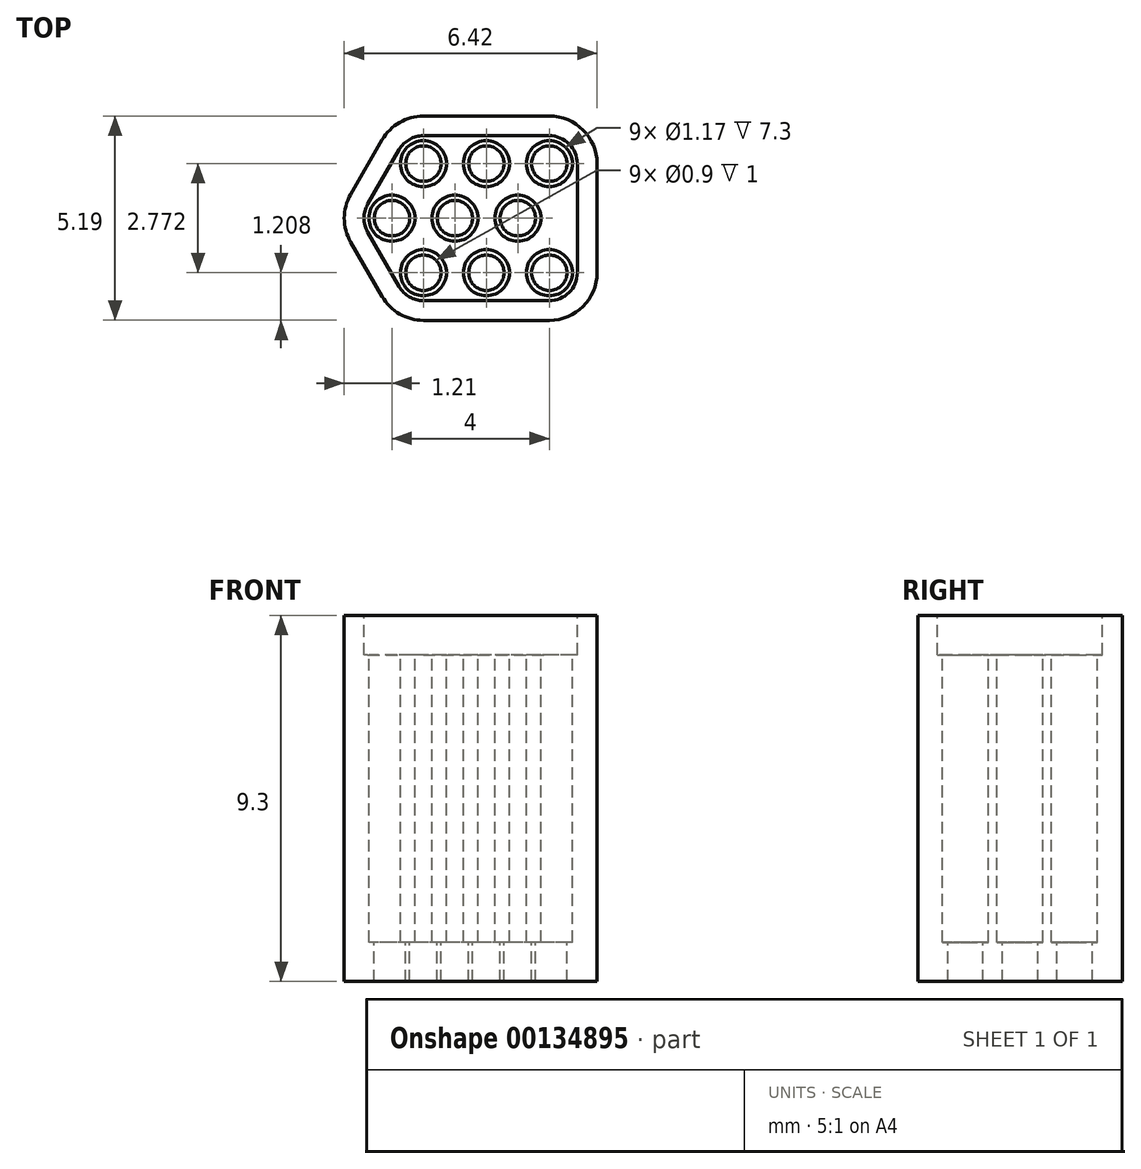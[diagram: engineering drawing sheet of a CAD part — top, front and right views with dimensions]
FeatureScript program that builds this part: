
annotation { "Feature Type Name" : "Feature", "Feature Type Description" : "" }
export const myFeature = defineFeature(function(context is Context, id is Id, definition is map)
    precondition{}
    {
        {
            var Q0;
            Q0=qCreatedBy(makeId("Top.planeOp"),FACE);
            var sketch = newSketch(context, id + "F0", { "sketchPlane" : qUnion([Q0])});
            skLineSegment(sketch, "E0", {"start": v(-0.8, 0) * mm, "end": v(-0.8, -4.2) * mm, "construction": true});
            skCircle(sketch, "E1", {"center": v(0, 0) * mm, "radius": 0.58 * mm});
            skCircle(sketch, "E2", {"center": v(0, -2.77) * mm, "radius": 0.58 * mm});
            skCircle(sketch, "E3", {"center": v(-0.8, -1.39) * mm, "radius": 0.58 * mm});
            skLineSegment(sketch, "E4", {"start": v(-4, -1.39) * mm, "end": v(-3.2, 0) * mm, "construction": true});
            skLineSegment(sketch, "E5", {"start": v(-3.2, 0) * mm, "end": v(0, 0) * mm, "construction": true});
            skLineSegment(sketch, "E6", {"start": v(0, 0) * mm, "end": v(0, -2.77) * mm, "construction": true});
            skLineSegment(sketch, "E7", {"start": v(-3.2, -2.77) * mm, "end": v(0, -2.77) * mm, "construction": true});
            skLineSegment(sketch, "E8", {"start": v(-3.2, -2.77) * mm, "end": v(-4, -1.39) * mm, "construction": true});
            skLineSegment(sketch, "E9.0", {"start": v(-3.6, -3.48) * mm, "end": v(-4.82, -1.39) * mm, "construction": true});
            skLineSegment(sketch, "E9.1", {"start": v(-3.6, 0.71) * mm, "end": v(0.71, 0.71) * mm, "construction": true});
            skLineSegment(sketch, "E9.2", {"start": v(0.71, 0.71) * mm, "end": v(0.71, -3.48) * mm, "construction": true});
            skLineSegment(sketch, "E9.3", {"start": v(-4.82, -1.39) * mm, "end": v(-3.6, 0.7) * mm, "construction": true});
            skLineSegment(sketch, "E9.5", {"start": v(-3.6, -3.48) * mm, "end": v(0.71, -3.48) * mm, "construction": true});
            skArc(sketch, "E10", {"start": v(-3.2, 0.7) * mm, "mid": v(-3.56, 0.61) * mm, "end": v(-3.81, 0.35) * mm});
            skArc(sketch, "E11", {"start": v(-4.61, -1.03) * mm, "mid": v(-4.71, -1.39) * mm, "end": v(-4.61, -1.74) * mm});
            skArc(sketch, "E12", {"start": v(-3.81, -3.13) * mm, "mid": v(-3.56, -3.39) * mm, "end": v(-3.2, -3.48) * mm});
            skArc(sketch, "E13", {"start": v(0, -3.48) * mm, "mid": v(0.5, -3.27) * mm, "end": v(0.7, -2.77) * mm});
            skArc(sketch, "E14", {"start": v(0.71, 0) * mm, "mid": v(0.5, 0.5) * mm, "end": v(0, 0.71) * mm});
            skLineSegment(sketch, "E15", {"start": v(-4.61, -1.03) * mm, "end": v(-3.81, 0.35) * mm});
            skLineSegment(sketch, "E16", {"start": v(-3.2, 0.71) * mm, "end": v(0, 0.71) * mm});
            skLineSegment(sketch, "E17", {"start": v(0.71, 0) * mm, "end": v(0.71, -2.77) * mm});
            skLineSegment(sketch, "E18", {"start": v(0, -3.48) * mm, "end": v(-3.2, -3.48) * mm});
            skLineSegment(sketch, "E19", {"start": v(-3.81, -3.13) * mm, "end": v(-4.61, -1.74) * mm});
            skArc(sketch, "E20.0", {"start": v(-3.2, 1.21) * mm, "mid": v(-3.8, 1.05) * mm, "end": v(-4.25, 0.6) * mm});
            skLineSegment(sketch, "E20.3", {"start": v(1.21, 0) * mm, "end": v(1.21, -2.77) * mm});
            skArc(sketch, "E20.4", {"start": v(1.21, 0) * mm, "mid": v(0.86, 0.86) * mm, "end": v(0, 1.21) * mm});
            skArc(sketch, "E20.5", {"start": v(0, -3.98) * mm, "mid": v(0.86, -3.63) * mm, "end": v(1.2, -2.77) * mm});
            skLineSegment(sketch, "E20.6", {"start": v(-3.2, 1.2) * mm, "end": v(0, 1.21) * mm});
            skLineSegment(sketch, "E20.7", {"start": v(0, -3.98) * mm, "end": v(-3.2, -3.98) * mm});
            skArc(sketch, "E20.8", {"start": v(-4.25, -3.38) * mm, "mid": v(-3.8, -3.82) * mm, "end": v(-3.2, -3.98) * mm});
            skLineSegment(sketch, "E20.9", {"start": v(-4.25, -3.38) * mm, "end": v(-5.05, -2) * mm});
            skArc(sketch, "E20.10", {"start": v(-5.05, -0.78) * mm, "mid": v(-5.2, -1.39) * mm, "end": v(-5.05, -2) * mm});
            skLineSegment(sketch, "E20.11", {"start": v(-5.05, -0.78) * mm, "end": v(-4.25, 0.6) * mm});
            skCircle(sketch, "E21.1.0.0", {"center": v(-1.6, -2.77) * mm, "radius": 0.58 * mm});
            skCircle(sketch, "E21.1.0.1", {"center": v(-2.4, -1.39) * mm, "radius": 0.58 * mm});
            skCircle(sketch, "E21.1.0.2", {"center": v(-1.6, 0) * mm, "radius": 0.58 * mm});
            skCircle(sketch, "E21.2.0.0", {"center": v(-3.2, -2.77) * mm, "radius": 0.58 * mm});
            skCircle(sketch, "E21.2.0.1", {"center": v(-4, -1.39) * mm, "radius": 0.58 * mm});
            skCircle(sketch, "E21.2.0.2", {"center": v(-3.2, 0) * mm, "radius": 0.58 * mm});
            skLineSegment(sketch, "E21.direction1", {"start": v(0, -2.77) * mm, "end": v(-1.6, -2.77) * mm, "construction": true});
            skSolve(sketch);
        }
        {
            var Q0;
            Q0=makeQuery(id+"F0.imprint","IMPRINT",FACE,{"disambiguationData":[TD([[makeQuery(id+"F0.imprint","IMPRINT",EDGE,{"derivedFrom":sQuery(id+"F0.wireOp",EDGE,"E10")}),-1.0]])]});
            var Q1;
            Q1=makeQuery(id+"F0.imprint","IMPRINT",FACE,{"disambiguationData":[TD([[makeQuery(id+"F0.imprint","IMPRINT",EDGE,{"derivedFrom":sQuery(id+"F0.wireOp",EDGE,"E1")}),-1.0]])]});
            var Q2;
            Q2=makeQuery(id+"F0.imprint","IMPRINT",FACE,{"disambiguationData":[TD([[makeQuery(id+"F0.imprint","IMPRINT",EDGE,{"derivedFrom":sQuery(id+"F0.wireOp",EDGE,"E21.2.0.1")}),1.0]])]});
            var Q3;
            Q3=makeQuery(id+"F0.imprint","IMPRINT",FACE,{"disambiguationData":[TD([[makeQuery(id+"F0.imprint","IMPRINT",EDGE,{"derivedFrom":sQuery(id+"F0.wireOp",EDGE,"E21.2.0.2")}),1.0]])]});
            var Q4;
            Q4=makeQuery(id+"F0.imprint","IMPRINT",FACE,{"disambiguationData":[TD([[makeQuery(id+"F0.imprint","IMPRINT",EDGE,{"derivedFrom":sQuery(id+"F0.wireOp",EDGE,"E21.1.0.2")}),1.0]])]});
            var Q5;
            Q5=makeQuery(id+"F0.imprint","IMPRINT",FACE,{"disambiguationData":[TD([[makeQuery(id+"F0.imprint","IMPRINT",EDGE,{"derivedFrom":sQuery(id+"F0.wireOp",EDGE,"E21.1.0.1")}),1.0]])]});
            var Q6;
            Q6=makeQuery(id+"F0.imprint","IMPRINT",FACE,{"disambiguationData":[TD([[makeQuery(id+"F0.imprint","IMPRINT",EDGE,{"derivedFrom":sQuery(id+"F0.wireOp",EDGE,"E21.2.0.0")}),1.0]])]});
            var Q7;
            Q7=makeQuery(id+"F0.imprint","IMPRINT",FACE,{"disambiguationData":[TD([[makeQuery(id+"F0.imprint","IMPRINT",EDGE,{"derivedFrom":sQuery(id+"F0.wireOp",EDGE,"E21.1.0.0")}),1.0]])]});
            var Q8;
            Q8=makeQuery(id+"F0.imprint","IMPRINT",FACE,{"disambiguationData":[TD([[makeQuery(id+"F0.imprint","IMPRINT",EDGE,{"derivedFrom":sQuery(id+"F0.wireOp",EDGE,"E3")}),1.0]])]});
            var Q9;
            Q9=makeQuery(id+"F0.imprint","IMPRINT",FACE,{"disambiguationData":[TD([[makeQuery(id+"F0.imprint","IMPRINT",EDGE,{"derivedFrom":sQuery(id+"F0.wireOp",EDGE,"E1")}),1.0]])]});
            var Q10;
            Q10=makeQuery(id+"F0.imprint","IMPRINT",FACE,{"disambiguationData":[TD([[makeQuery(id+"F0.imprint","IMPRINT",EDGE,{"derivedFrom":sQuery(id+"F0.wireOp",EDGE,"E2")}),1.0]])]});
            extrude(context, id + "F1", {"entities" : qUnion([Q0, Q1, Q2, Q3, Q4, Q5, Q6, Q7, Q8, Q9, Q10]), "oppositeDirection" : true, "depth" : 9.3 * mm});
        }
        {
            var Q0;
            Q0=makeQuery(id+"F0.imprint","IMPRINT",FACE,{"disambiguationData":[TD([[makeQuery(id+"F0.imprint","IMPRINT",EDGE,{"derivedFrom":sQuery(id+"F0.wireOp",EDGE,"E1")}),-1.0]])]});
            var Q1;
            Q1=makeQuery(id+"F0.imprint","IMPRINT",FACE,{"disambiguationData":[TD([[makeQuery(id+"F0.imprint","IMPRINT",EDGE,{"derivedFrom":sQuery(id+"F0.wireOp",EDGE,"a57e1848-316f-4acb-9686-28404833bcae.3.0.0")}),1.0]])]});
            var Q2;
            Q2=makeQuery(id+"F0.imprint","IMPRINT",FACE,{"disambiguationData":[TD([[makeQuery(id+"F0.imprint","IMPRINT",EDGE,{"derivedFrom":sQuery(id+"F0.wireOp",EDGE,"a57e1848-316f-4acb-9686-28404833bcae.3.0.1")}),1.0]])]});
            var Q3;
            Q3=makeQuery(id+"F0.imprint","IMPRINT",FACE,{"disambiguationData":[TD([[makeQuery(id+"F0.imprint","IMPRINT",EDGE,{"derivedFrom":sQuery(id+"F0.wireOp",EDGE,"e6241aa5-61be-4e4d-b619-a7d30d87e54e.1.0.0")}),1.0]])]});
            var Q4;
            Q4=makeQuery(id+"F0.imprint","IMPRINT",FACE,{"disambiguationData":[TD([[makeQuery(id+"F0.imprint","IMPRINT",EDGE,{"derivedFrom":sQuery(id+"F0.wireOp",EDGE,"a57e1848-316f-4acb-9686-28404833bcae.3.0.2")}),1.0]])]});
            var Q5;
            Q5=makeQuery(id+"F0.imprint","IMPRINT",FACE,{"disambiguationData":[TD([[makeQuery(id+"F0.imprint","IMPRINT",EDGE,{"derivedFrom":sQuery(id+"F0.wireOp",EDGE,"a57e1848-316f-4acb-9686-28404833bcae.3.0.3")}),1.0]])]});
            var Q6;
            Q6=makeQuery(id+"F0.imprint","IMPRINT",FACE,{"disambiguationData":[TD([[makeQuery(id+"F0.imprint","IMPRINT",EDGE,{"derivedFrom":sQuery(id+"F0.wireOp",EDGE,"a57e1848-316f-4acb-9686-28404833bcae.2.0.2")}),1.0]])]});
            var Q7;
            Q7=makeQuery(id+"F0.imprint","IMPRINT",FACE,{"disambiguationData":[TD([[makeQuery(id+"F0.imprint","IMPRINT",EDGE,{"derivedFrom":sQuery(id+"F0.wireOp",EDGE,"a57e1848-316f-4acb-9686-28404833bcae.2.0.1")}),1.0]])]});
            var Q8;
            Q8=makeQuery(id+"F0.imprint","IMPRINT",FACE,{"disambiguationData":[TD([[makeQuery(id+"F0.imprint","IMPRINT",EDGE,{"derivedFrom":sQuery(id+"F0.wireOp",EDGE,"a57e1848-316f-4acb-9686-28404833bcae.2.0.0")}),1.0]])]});
            var Q9;
            Q9=makeQuery(id+"F0.imprint","IMPRINT",FACE,{"disambiguationData":[TD([[makeQuery(id+"F0.imprint","IMPRINT",EDGE,{"derivedFrom":sQuery(id+"F0.wireOp",EDGE,"a57e1848-316f-4acb-9686-28404833bcae.1.0.0")}),1.0]])]});
            var Q10;
            Q10=makeQuery(id+"F0.imprint","IMPRINT",FACE,{"disambiguationData":[TD([[makeQuery(id+"F0.imprint","IMPRINT",EDGE,{"derivedFrom":sQuery(id+"F0.wireOp",EDGE,"a57e1848-316f-4acb-9686-28404833bcae.1.0.1")}),1.0]])]});
            var Q11;
            Q11=makeQuery(id+"F0.imprint","IMPRINT",FACE,{"disambiguationData":[TD([[makeQuery(id+"F0.imprint","IMPRINT",EDGE,{"derivedFrom":sQuery(id+"F0.wireOp",EDGE,"a57e1848-316f-4acb-9686-28404833bcae.2.0.3")}),1.0]])]});
            var Q12;
            Q12=makeQuery(id+"F0.imprint","IMPRINT",FACE,{"disambiguationData":[TD([[makeQuery(id+"F0.imprint","IMPRINT",EDGE,{"derivedFrom":sQuery(id+"F0.wireOp",EDGE,"a57e1848-316f-4acb-9686-28404833bcae.1.0.2")}),1.0]])]});
            var Q13;
            Q13=makeQuery(id+"F0.imprint","IMPRINT",FACE,{"disambiguationData":[TD([[makeQuery(id+"F0.imprint","IMPRINT",EDGE,{"derivedFrom":sQuery(id+"F0.wireOp",EDGE,"E1")}),1.0]])]});
            var Q14;
            Q14=makeQuery(id+"F0.imprint","IMPRINT",FACE,{"disambiguationData":[TD([[makeQuery(id+"F0.imprint","IMPRINT",EDGE,{"derivedFrom":sQuery(id+"F0.wireOp",EDGE,"E3")}),1.0]])]});
            var Q15;
            Q15=makeQuery(id+"F0.imprint","IMPRINT",FACE,{"disambiguationData":[TD([[makeQuery(id+"F0.imprint","IMPRINT",EDGE,{"derivedFrom":sQuery(id+"F0.wireOp",EDGE,"a57e1848-316f-4acb-9686-28404833bcae.1.0.3")}),1.0]])]});
            var Q16;
            Q16=makeQuery(id+"F0.imprint","IMPRINT",FACE,{"disambiguationData":[TD([[makeQuery(id+"F0.imprint","IMPRINT",EDGE,{"derivedFrom":sQuery(id+"F0.wireOp",EDGE,"nBaw7tlR-HIxs-2q5P-bhm3-oVcILwCY4JMG")}),1.0]])]});
            var Q17;
            Q17=makeQuery(id+"F0.imprint","IMPRINT",FACE,{"disambiguationData":[TD([[makeQuery(id+"F0.imprint","IMPRINT",EDGE,{"derivedFrom":sQuery(id+"F0.wireOp",EDGE,"E2")}),1.0]])]});
            var Q18;
            Q18=makeQuery(id+"F0.imprint","IMPRINT",FACE,{"disambiguationData":[TD([[makeQuery(id+"F0.imprint","IMPRINT",EDGE,{"derivedFrom":sQuery(id+"F0.wireOp",EDGE,"E21.2.0.1")}),1.0]])]});
            var Q19;
            Q19=makeQuery(id+"F0.imprint","IMPRINT",FACE,{"disambiguationData":[TD([[makeQuery(id+"F0.imprint","IMPRINT",EDGE,{"derivedFrom":sQuery(id+"F0.wireOp",EDGE,"E21.1.0.1")}),1.0]])]});
            var Q20;
            Q20=makeQuery(id+"F0.imprint","IMPRINT",FACE,{"disambiguationData":[TD([[makeQuery(id+"F0.imprint","IMPRINT",EDGE,{"derivedFrom":sQuery(id+"F0.wireOp",EDGE,"E21.2.0.2")}),1.0]])]});
            var Q21;
            Q21=makeQuery(id+"F0.imprint","IMPRINT",FACE,{"disambiguationData":[TD([[makeQuery(id+"F0.imprint","IMPRINT",EDGE,{"derivedFrom":sQuery(id+"F0.wireOp",EDGE,"E21.1.0.2")}),1.0]])]});
            var Q22;
            Q22=makeQuery(id+"F0.imprint","IMPRINT",FACE,{"disambiguationData":[TD([[makeQuery(id+"F0.imprint","IMPRINT",EDGE,{"derivedFrom":sQuery(id+"F0.wireOp",EDGE,"E21.1.0.0")}),1.0]])]});
            var Q23;
            Q23=makeQuery(id+"F0.imprint","IMPRINT",FACE,{"disambiguationData":[TD([[makeQuery(id+"F0.imprint","IMPRINT",EDGE,{"derivedFrom":sQuery(id+"F0.wireOp",EDGE,"E21.2.0.0")}),1.0]])]});
            extrude(context, id + "F2", {"entities" : qUnion([Q0, Q1, Q2, Q3, Q4, Q5, Q6, Q7, Q8, Q9, Q10, Q11, Q12, Q13, Q14, Q15, Q16, Q17, Q18, Q19, Q20, Q21, Q22, Q23]), "operationType" : NewBodyOperationType.REMOVE, "oppositeDirection" : true, "depth" : 1 * mm});
        }
        {
            var Q0;
            Q0=makeQuery(id+"F0.imprint","IMPRINT",FACE,{"disambiguationData":[TD([[makeQuery(id+"F0.imprint","IMPRINT",EDGE,{"derivedFrom":sQuery(id+"F0.wireOp",EDGE,"e6241aa5-61be-4e4d-b619-a7d30d87e54e.1.0.0")}),1.0]])]});
            var Q1;
            Q1=makeQuery(id+"F0.imprint","IMPRINT",FACE,{"disambiguationData":[TD([[makeQuery(id+"F0.imprint","IMPRINT",EDGE,{"derivedFrom":sQuery(id+"F0.wireOp",EDGE,"a57e1848-316f-4acb-9686-28404833bcae.3.0.1")}),1.0]])]});
            var Q2;
            Q2=makeQuery(id+"F0.imprint","IMPRINT",FACE,{"disambiguationData":[TD([[makeQuery(id+"F0.imprint","IMPRINT",EDGE,{"derivedFrom":sQuery(id+"F0.wireOp",EDGE,"a57e1848-316f-4acb-9686-28404833bcae.3.0.0")}),1.0]])]});
            var Q3;
            Q3=makeQuery(id+"F0.imprint","IMPRINT",FACE,{"disambiguationData":[TD([[makeQuery(id+"F0.imprint","IMPRINT",EDGE,{"derivedFrom":sQuery(id+"F0.wireOp",EDGE,"a57e1848-316f-4acb-9686-28404833bcae.3.0.2")}),1.0]])]});
            var Q4;
            Q4=makeQuery(id+"F0.imprint","IMPRINT",FACE,{"disambiguationData":[TD([[makeQuery(id+"F0.imprint","IMPRINT",EDGE,{"derivedFrom":sQuery(id+"F0.wireOp",EDGE,"a57e1848-316f-4acb-9686-28404833bcae.3.0.3")}),1.0]])]});
            var Q5;
            Q5=makeQuery(id+"F0.imprint","IMPRINT",FACE,{"disambiguationData":[TD([[makeQuery(id+"F0.imprint","IMPRINT",EDGE,{"derivedFrom":sQuery(id+"F0.wireOp",EDGE,"a57e1848-316f-4acb-9686-28404833bcae.2.0.1")}),1.0]])]});
            var Q6;
            Q6=makeQuery(id+"F0.imprint","IMPRINT",FACE,{"disambiguationData":[TD([[makeQuery(id+"F0.imprint","IMPRINT",EDGE,{"derivedFrom":sQuery(id+"F0.wireOp",EDGE,"a57e1848-316f-4acb-9686-28404833bcae.2.0.0")}),1.0]])]});
            var Q7;
            Q7=makeQuery(id+"F0.imprint","IMPRINT",FACE,{"disambiguationData":[TD([[makeQuery(id+"F0.imprint","IMPRINT",EDGE,{"derivedFrom":sQuery(id+"F0.wireOp",EDGE,"a57e1848-316f-4acb-9686-28404833bcae.1.0.0")}),1.0]])]});
            var Q8;
            Q8=makeQuery(id+"F0.imprint","IMPRINT",FACE,{"disambiguationData":[TD([[makeQuery(id+"F0.imprint","IMPRINT",EDGE,{"derivedFrom":sQuery(id+"F0.wireOp",EDGE,"a57e1848-316f-4acb-9686-28404833bcae.1.0.1")}),1.0]])]});
            var Q9;
            Q9=makeQuery(id+"F0.imprint","IMPRINT",FACE,{"disambiguationData":[TD([[makeQuery(id+"F0.imprint","IMPRINT",EDGE,{"derivedFrom":sQuery(id+"F0.wireOp",EDGE,"a57e1848-316f-4acb-9686-28404833bcae.2.0.3")}),1.0]])]});
            var Q10;
            Q10=makeQuery(id+"F0.imprint","IMPRINT",FACE,{"disambiguationData":[TD([[makeQuery(id+"F0.imprint","IMPRINT",EDGE,{"derivedFrom":sQuery(id+"F0.wireOp",EDGE,"a57e1848-316f-4acb-9686-28404833bcae.2.0.2")}),1.0]])]});
            var Q11;
            Q11=makeQuery(id+"F0.imprint","IMPRINT",FACE,{"disambiguationData":[TD([[makeQuery(id+"F0.imprint","IMPRINT",EDGE,{"derivedFrom":sQuery(id+"F0.wireOp",EDGE,"a57e1848-316f-4acb-9686-28404833bcae.1.0.2")}),1.0]])]});
            var Q12;
            Q12=makeQuery(id+"F0.imprint","IMPRINT",FACE,{"disambiguationData":[TD([[makeQuery(id+"F0.imprint","IMPRINT",EDGE,{"derivedFrom":sQuery(id+"F0.wireOp",EDGE,"a57e1848-316f-4acb-9686-28404833bcae.1.0.3")}),1.0]])]});
            var Q13;
            Q13=makeQuery(id+"F0.imprint","IMPRINT",FACE,{"disambiguationData":[TD([[makeQuery(id+"F0.imprint","IMPRINT",EDGE,{"derivedFrom":sQuery(id+"F0.wireOp",EDGE,"E3")}),1.0]])]});
            var Q14;
            Q14=makeQuery(id+"F0.imprint","IMPRINT",FACE,{"disambiguationData":[TD([[makeQuery(id+"F0.imprint","IMPRINT",EDGE,{"derivedFrom":sQuery(id+"F0.wireOp",EDGE,"E1")}),1.0]])]});
            var Q15;
            Q15=makeQuery(id+"F0.imprint","IMPRINT",FACE,{"disambiguationData":[TD([[makeQuery(id+"F0.imprint","IMPRINT",EDGE,{"derivedFrom":sQuery(id+"F0.wireOp",EDGE,"E2")}),1.0]])]});
            var Q16;
            Q16=makeQuery(id+"F0.imprint","IMPRINT",FACE,{"disambiguationData":[TD([[makeQuery(id+"F0.imprint","IMPRINT",EDGE,{"derivedFrom":sQuery(id+"F0.wireOp",EDGE,"nBaw7tlR-HIxs-2q5P-bhm3-oVcILwCY4JMG")}),1.0]])]});
            var Q17;
            Q17=makeQuery(id+"F0.imprint","IMPRINT",FACE,{"disambiguationData":[TD([[makeQuery(id+"F0.imprint","IMPRINT",EDGE,{"derivedFrom":sQuery(id+"F0.wireOp",EDGE,"nBaw7tlR-HIxs-2q5P-bhm3-oVcILwCY4JMG")}),1.0]])]});
            var Q18;
            Q18=makeQuery(id+"F0.imprint","IMPRINT",FACE,{"disambiguationData":[TD([[makeQuery(id+"F0.imprint","IMPRINT",EDGE,{"derivedFrom":sQuery(id+"F0.wireOp",EDGE,"a57e1848-316f-4acb-9686-28404833bcae.2.0.2")}),1.0]])]});
            var Q19;
            Q19=makeQuery(id+"F0.imprint","IMPRINT",FACE,{"disambiguationData":[TD([[makeQuery(id+"F0.imprint","IMPRINT",EDGE,{"derivedFrom":sQuery(id+"F0.wireOp",EDGE,"a57e1848-316f-4acb-9686-28404833bcae.1.0.2")}),1.0]])]});
            var Q20;
            Q20=makeQuery(id+"F0.imprint","IMPRINT",FACE,{"disambiguationData":[TD([[makeQuery(id+"F0.imprint","IMPRINT",EDGE,{"derivedFrom":sQuery(id+"F0.wireOp",EDGE,"a57e1848-316f-4acb-9686-28404833bcae.1.0.3")}),1.0]])]});
            var Q21;
            Q21=makeQuery(id+"F0.imprint","IMPRINT",FACE,{"disambiguationData":[TD([[makeQuery(id+"F0.imprint","IMPRINT",EDGE,{"derivedFrom":sQuery(id+"F0.wireOp",EDGE,"E3")}),1.0]])]});
            var Q22;
            Q22=makeQuery(id+"F0.imprint","IMPRINT",FACE,{"disambiguationData":[TD([[makeQuery(id+"F0.imprint","IMPRINT",EDGE,{"derivedFrom":sQuery(id+"F0.wireOp",EDGE,"E1")}),1.0]])]});
            var Q23;
            Q23=makeQuery(id+"F0.imprint","IMPRINT",FACE,{"disambiguationData":[TD([[makeQuery(id+"F0.imprint","IMPRINT",EDGE,{"derivedFrom":sQuery(id+"F0.wireOp",EDGE,"E2")}),1.0]])]});
            var Q24;
            Q24=makeQuery(id+"F0.imprint","IMPRINT",FACE,{"disambiguationData":[TD([[makeQuery(id+"F0.imprint","IMPRINT",EDGE,{"derivedFrom":sQuery(id+"F0.wireOp",EDGE,"nBaw7tlR-HIxs-2q5P-bhm3-oVcILwCY4JMG")}),1.0]])]});
            var Q25;
            Q25=makeQuery(id+"F0.imprint","IMPRINT",FACE,{"disambiguationData":[TD([[makeQuery(id+"F0.imprint","IMPRINT",EDGE,{"derivedFrom":sQuery(id+"F0.wireOp",EDGE,"E21.1.0.0")}),1.0]])]});
            var Q26;
            Q26=makeQuery(id+"F0.imprint","IMPRINT",FACE,{"disambiguationData":[TD([[makeQuery(id+"F0.imprint","IMPRINT",EDGE,{"derivedFrom":sQuery(id+"F0.wireOp",EDGE,"E21.2.0.0")}),1.0]])]});
            var Q27;
            Q27=makeQuery(id+"F0.imprint","IMPRINT",FACE,{"disambiguationData":[TD([[makeQuery(id+"F0.imprint","IMPRINT",EDGE,{"derivedFrom":sQuery(id+"F0.wireOp",EDGE,"E21.1.0.1")}),1.0]])]});
            var Q28;
            Q28=makeQuery(id+"F0.imprint","IMPRINT",FACE,{"disambiguationData":[TD([[makeQuery(id+"F0.imprint","IMPRINT",EDGE,{"derivedFrom":sQuery(id+"F0.wireOp",EDGE,"E21.1.0.2")}),1.0]])]});
            var Q29;
            Q29=makeQuery(id+"F0.imprint","IMPRINT",FACE,{"disambiguationData":[TD([[makeQuery(id+"F0.imprint","IMPRINT",EDGE,{"derivedFrom":sQuery(id+"F0.wireOp",EDGE,"E21.2.0.2")}),1.0]])]});
            var Q30;
            Q30=makeQuery(id+"F0.imprint","IMPRINT",FACE,{"disambiguationData":[TD([[makeQuery(id+"F0.imprint","IMPRINT",EDGE,{"derivedFrom":sQuery(id+"F0.wireOp",EDGE,"E21.2.0.1")}),1.0]])]});
            extrude(context, id + "F3", {"entities" : qUnion([Q0, Q1, Q2, Q3, Q4, Q5, Q6, Q7, Q8, Q9, Q10, Q11, Q12, Q13, Q14, Q15, Q16, Q17, Q18, Q19, Q20, Q21, Q22, Q23, Q24, Q25, Q26, Q27, Q28, Q29, Q30]), "operationType" : NewBodyOperationType.REMOVE, "oppositeDirection" : true, "depth" : 8.3 * mm});
        }
        {
            var Q0;
            Q0=qCreatedBy(makeId("Top.planeOp"),FACE);
            var sketch = newSketch(context, id + "F4", { "sketchPlane" : qUnion([Q0])});
            skLineSegment(sketch, "E22", {"start": v(-0.8, 0) * mm, "end": v(-0.8, -4.16) * mm, "construction": true});
            skCircle(sketch, "E23", {"center": v(0, 0) * mm, "radius": 0.58 * mm, "construction": true});
            skCircle(sketch, "E24", {"center": v(0, -2.77) * mm, "radius": 0.58 * mm, "construction": true});
            skCircle(sketch, "E25", {"center": v(-0.8, -1.39) * mm, "radius": 0.58 * mm, "construction": true});
            skCircle(sketch, "E26", {"center": v(-0.8, -4.16) * mm, "radius": 0.58 * mm, "construction": true});
            skCircle(sketch, "E27.1.0.0", {"center": v(-1.6, 0) * mm, "radius": 0.58 * mm, "construction": true});
            skCircle(sketch, "E27.1.0.1", {"center": v(-2.4, -1.39) * mm, "radius": 0.58 * mm, "construction": true});
            skCircle(sketch, "E27.1.0.2", {"center": v(-2.4, -4.16) * mm, "radius": 0.58 * mm, "construction": true});
            skCircle(sketch, "E27.1.0.3", {"center": v(-1.6, -2.77) * mm, "radius": 0.58 * mm, "construction": true});
            skCircle(sketch, "E27.2.0.0", {"center": v(-3.2, 0) * mm, "radius": 0.58 * mm, "construction": true});
            skCircle(sketch, "E27.2.0.1", {"center": v(-4, -1.39) * mm, "radius": 0.58 * mm, "construction": true});
            skCircle(sketch, "E27.2.0.2", {"center": v(-4, -4.16) * mm, "radius": 0.58 * mm, "construction": true});
            skCircle(sketch, "E27.2.0.3", {"center": v(-3.2, -2.77) * mm, "radius": 0.58 * mm, "construction": true});
            skCircle(sketch, "E27.3.0.0", {"center": v(-4.8, 0) * mm, "radius": 0.58 * mm, "construction": true});
            skCircle(sketch, "E27.3.0.1", {"center": v(-5.6, -1.39) * mm, "radius": 0.58 * mm, "construction": true});
            skCircle(sketch, "E27.3.0.2", {"center": v(-5.6, -4.16) * mm, "radius": 0.58 * mm, "construction": true});
            skCircle(sketch, "E27.3.0.3", {"center": v(-4.8, -2.77) * mm, "radius": 0.58 * mm, "construction": true});
            skLineSegment(sketch, "E27.direction1", {"start": v(-0.8, -4.16) * mm, "end": v(-2.4, -4.16) * mm, "construction": true});
            skCircle(sketch, "E28.1.0.0", {"center": v(-6.4, -2.77) * mm, "radius": 0.58 * mm, "construction": true});
            skLineSegment(sketch, "E28.direction1", {"start": v(-4.8, -2.77) * mm, "end": v(-6.4, -2.77) * mm, "construction": true});
            skCircle(sketch, "E29", {"center": v(0, 0) * mm, "radius": 0.45 * mm});
            skCircle(sketch, "E30", {"center": v(-0.8, -1.39) * mm, "radius": 0.45 * mm});
            skCircle(sketch, "E31", {"center": v(0, -2.77) * mm, "radius": 0.45 * mm});
            skCircle(sketch, "E32", {"center": v(-0.8, -4.16) * mm, "radius": 0.45 * mm});
            skCircle(sketch, "E33.1.0.0", {"center": v(-1.6, 0) * mm, "radius": 0.45 * mm});
            skCircle(sketch, "E33.1.0.1", {"center": v(-2.4, -1.39) * mm, "radius": 0.45 * mm});
            skCircle(sketch, "E33.1.0.2", {"center": v(-1.6, -2.77) * mm, "radius": 0.45 * mm});
            skCircle(sketch, "E33.1.0.3", {"center": v(-2.4, -4.16) * mm, "radius": 0.45 * mm});
            skCircle(sketch, "E33.2.0.0", {"center": v(-3.2, 0) * mm, "radius": 0.45 * mm});
            skCircle(sketch, "E33.2.0.1", {"center": v(-4, -1.39) * mm, "radius": 0.45 * mm});
            skCircle(sketch, "E33.2.0.2", {"center": v(-3.2, -2.77) * mm, "radius": 0.45 * mm});
            skCircle(sketch, "E33.2.0.3", {"center": v(-4, -4.16) * mm, "radius": 0.45 * mm});
            skCircle(sketch, "E33.3.0.0", {"center": v(-4.8, 0) * mm, "radius": 0.45 * mm});
            skCircle(sketch, "E33.3.0.1", {"center": v(-5.6, -1.39) * mm, "radius": 0.45 * mm});
            skCircle(sketch, "E33.3.0.2", {"center": v(-4.8, -2.77) * mm, "radius": 0.45 * mm});
            skCircle(sketch, "E33.3.0.3", {"center": v(-5.6, -4.16) * mm, "radius": 0.45 * mm});
            skCircle(sketch, "E34.1.0.0", {"center": v(-6.4, -2.77) * mm, "radius": 0.45 * mm});
            skSolve(sketch);
        }
        {
            var Q0;
            Q0=makeQuery(id+"F4.imprint","IMPRINT",FACE,{"disambiguationData":[TD([[makeQuery(id+"F4.imprint","IMPRINT",EDGE,{"derivedFrom":sQuery(id+"F4.wireOp",EDGE,"E33.2.0.0")}),1.0]])]});
            var Q1;
            Q1=makeQuery(id+"F4.imprint","IMPRINT",FACE,{"disambiguationData":[TD([[makeQuery(id+"F4.imprint","IMPRINT",EDGE,{"derivedFrom":sQuery(id+"F4.wireOp",EDGE,"E33.1.0.0")}),1.0]])]});
            var Q2;
            Q2=makeQuery(id+"F4.imprint","IMPRINT",FACE,{"disambiguationData":[TD([[makeQuery(id+"F4.imprint","IMPRINT",EDGE,{"derivedFrom":sQuery(id+"F4.wireOp",EDGE,"E29")}),1.0]])]});
            var Q3;
            Q3=makeQuery(id+"F4.imprint","IMPRINT",FACE,{"disambiguationData":[TD([[makeQuery(id+"F4.imprint","IMPRINT",EDGE,{"derivedFrom":sQuery(id+"F4.wireOp",EDGE,"E30")}),1.0]])]});
            var Q4;
            Q4=makeQuery(id+"F4.imprint","IMPRINT",FACE,{"disambiguationData":[TD([[makeQuery(id+"F4.imprint","IMPRINT",EDGE,{"derivedFrom":sQuery(id+"F4.wireOp",EDGE,"E33.1.0.1")}),1.0]])]});
            var Q5;
            Q5=makeQuery(id+"F4.imprint","IMPRINT",FACE,{"disambiguationData":[TD([[makeQuery(id+"F4.imprint","IMPRINT",EDGE,{"derivedFrom":sQuery(id+"F4.wireOp",EDGE,"E33.2.0.1")}),1.0]])]});
            var Q6;
            Q6=makeQuery(id+"F4.imprint","IMPRINT",FACE,{"disambiguationData":[TD([[makeQuery(id+"F4.imprint","IMPRINT",EDGE,{"derivedFrom":sQuery(id+"F4.wireOp",EDGE,"E33.2.0.2")}),1.0]])]});
            var Q7;
            Q7=makeQuery(id+"F4.imprint","IMPRINT",FACE,{"disambiguationData":[TD([[makeQuery(id+"F4.imprint","IMPRINT",EDGE,{"derivedFrom":sQuery(id+"F4.wireOp",EDGE,"E33.1.0.2")}),1.0]])]});
            var Q8;
            Q8=makeQuery(id+"F4.imprint","IMPRINT",FACE,{"disambiguationData":[TD([[makeQuery(id+"F4.imprint","IMPRINT",EDGE,{"derivedFrom":sQuery(id+"F4.wireOp",EDGE,"E31")}),1.0]])]});
            extrude(context, id + "F5", {"entities" : qUnion([Q0, Q1, Q2, Q3, Q4, Q5, Q6, Q7, Q8]), "operationType" : NewBodyOperationType.REMOVE, "endBound" : BoundingType.THROUGH_ALL, "oppositeDirection" : true, "depth" : 25 * mm});
        }
    });
